# Revit family: Dozownik_mydla_w_pianie 1l HIT
name_source: partatom
category: Furniture
units: mm (PartAtom-declared; Revit-internal decimal feet)

## family parameters
Always vertical = Yes
Cut with Voids When Loaded = No
Host = Wall
Room Calculation Point = No
Shared = No

## types (1)
- SF1002SJB
    Depth / Glebokosc = 100 mm  [stored 0.328084 ft]
    Description = Dozownik mydła w pianie 1 l HIT jest bardzo mocnym i odpornym na uszkodzenia naściennym podajnikiem, który wykonano ze stali nierdzewnej matowej. To elegancki, nowoczesny i funkcjonalny element wyposażenia toalet publicznych. Dzięki dużej pojemności świetnie pasuje do pomieszczeń o wysokim natężeniu ruchu. Okienko umożliwia sprawne kontrolowanie poziomu mydła wewnątrz dozownika, a ergonomiczny przycisk gwarantuje komfort jego użytkowania.
    Height / Wysokosc = 280 mm  [stored 0.918635 ft]
    Manufacturer = FANECO.com
    Manufacturer code / Kod producenta = 5901764295846
    Material = Stal nierdzewna szczotkowana
    Material finish / Wykonczenie = Stal nierdzewna 304 szczotkowana
    Model = HIT
    Product code / Kod produktu = SF1002SJB
    Type Comments = Dozownik mydła w pianie 1l HIT
    URL = https://faneco.com
    Weight / Waga = 1.05 kg
    Width / Szerokosc = 100 mm  [stored 0.328084 ft]

note: [stored X ft] marks values corroborated as IEEE doubles in the binary element streams (Revit-internal decimal feet)

## geometry (parser evidence)
native form markers: Sweep x8
no freeform markers — native parametric forms only
